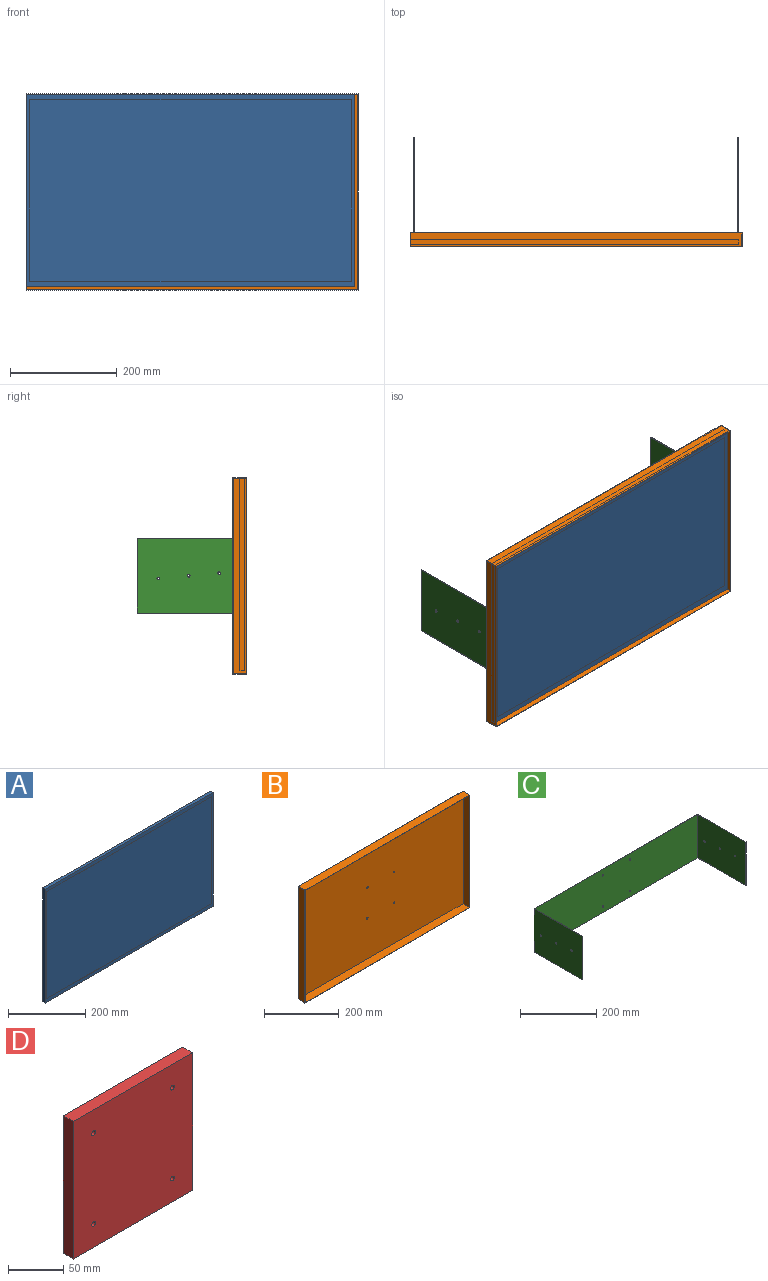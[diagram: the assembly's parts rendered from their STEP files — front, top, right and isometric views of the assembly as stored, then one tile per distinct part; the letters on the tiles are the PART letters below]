
ASSEMBLY  parts=4 mates=9
PART A: 11 faces, bbox 615.4x8.6x361.1 mm
  f0: plane 615.44x361.06mm, normal (0,1,0), area 222212.1mm2, adj f5,f6,f7,f8
  f1: plane 339.73x0.25mm, normal (1,0,0), area 86.3mm2, adj f2,f4,f9,f10
  f2: plane 603.25x0.25mm, normal (0,0,1), area 153.2mm2, adj f1,f3,f9,f10
  f3: plane 339.73x0.25mm, normal (-1,0,0), area 86.3mm2, adj f2,f4,f9,f10
  f4: plane 603.25x0.25mm, normal (0,0,-1), area 153.2mm2, adj f1,f3,f9,f10
  f5: plane 361.06x8.57mm, normal (-1,0,0), area 3095.2mm2, adj f0,f6,f8,f9
  f6: plane 615.44x8.57mm, normal (0,0,-1), area 5275.9mm2, adj f0,f5,f7,f9
  f7: plane 361.06x8.57mm, normal (1,0,0), area 3095.2mm2, adj f0,f6,f8,f9
  f8: plane 615.44x8.57mm, normal (0,0,1), area 5275.9mm2, adj f0,f5,f7,f9
  f9: plane 615.44x361.06mm, normal (0,-1,0), area 17273mm2, adj f1,f2,f3,f4,f5,f6,f7,f8
  f10: plane 603.25x339.73mm, normal (0,-1,0), area 204939.1mm2, adj f1,f2,f3,f4
PART B: 15 faces, bbox 622.3x26.2x368.3 mm
  f0: plane 622.3x26.16mm, normal (0,0,-1), area 16280.6mm2, adj f1,f3,f4,f9
  f1: plane 368.3x26.16mm, normal (1,0,0), area 9635.5mm2, adj f0,f2,f4,f9
  f2: plane 622.3x26.16mm, normal (0,0,1), area 16280.6mm2, adj f1,f3,f4,f9
  f3: plane 368.3x26.16mm, normal (-1,0,0), area 9635.5mm2, adj f0,f2,f4,f9
  f4: plane 622.3x368.3mm, normal (0,1,0), area 229121.8mm2, adj f0,f1,f2,f3,f11,f12,f13,f14
  f5: plane 620.78x25.4mm, normal (0,0,1), area 15767.7mm2, adj f6,f8,f9,f10
  f6: plane 366.78x25.4mm, normal (1,0,0), area 9316.1mm2, adj f5,f7,f9,f10
  f7: plane 620.78x25.4mm, normal (0,0,-1), area 15767.7mm2, adj f6,f8,f9,f10
  f8: plane 366.78x25.4mm, normal (-1,0,0), area 9316.1mm2, adj f5,f7,f9,f10
  f9: plane 622.3x368.3mm, normal (0,-1,0), area 1507.4mm2, adj f0,f1,f2,f3,f5,f6,f7,f8
  f10: plane 620.78x366.78mm, normal (0,-1,0), area 227614.5mm2, adj f5,f6,f7,f8,f11,f12,f13,f14
  f11: cylinder r=2.38mm len=4.76mm, axis (0,1,0), area 11.4mm2, adj f4,f10
  f12: cylinder r=2.38mm len=4.76mm, axis (0,1,0), area 11.4mm2, adj f4,f10
  f13: cylinder r=2.38mm len=4.76mm, axis (0,1,0), area 11.4mm2, adj f4,f10
  f14: cylinder r=2.38mm len=4.76mm, axis (0,1,0), area 11.4mm2, adj f4,f10
PART C: 20 faces, bbox 609.6x179x139.7 mm
  f0: plane 607.16x139.7mm, normal (0,-1,0), area 84749.2mm2, adj f2,f4,f6,f7,f8,f9,f10,f13
  f1: plane 179.02x139.7mm, normal (-1,0,0), area 24955.5mm2, adj f2,f4,f5,f11,f17,f18,f19
  f2: plane 609.6x179.02mm, normal (0,0,-1), area 1176.8mm2, adj f0,f1,f3,f5,f10,f11,f12,f13
  f3: plane 179.02x139.7mm, normal (1,0,0), area 24955.5mm2, adj f2,f4,f5,f12,f14,f15,f16
  f4: plane 609.6x179.02mm, normal (0,0,1), area 1176.8mm2, adj f0,f1,f3,f5,f10,f11,f12,f13
  f5: plane 609.6x139.7mm, normal (0,1,0), area 85089.9mm2, adj f1,f2,f3,f4,f6,f7,f8,f9
  f6: cylinder r=2.38mm len=4.76mm, axis (0,-1,0), area 18.2mm2, adj f0,f5
  f7: cylinder r=2.38mm len=4.76mm, axis (0,-1,0), area 18.2mm2, adj f0,f5
  f8: cylinder r=2.38mm len=4.76mm, axis (0,-1,0), area 18.2mm2, adj f0,f5
  f9: cylinder r=2.38mm len=4.76mm, axis (0,-1,0), area 18.2mm2, adj f0,f5
  f10: plane 177.8x139.7mm, normal (1,0,0), area 24785.2mm2, adj f0,f2,f4,f11,f17,f18,f19
  f11: plane 139.7x1.22mm, normal (0,-1,0), area 170.3mm2, adj f1,f2,f4,f10
  f12: plane 139.7x1.22mm, normal (0,-1,0), area 170.3mm2, adj f2,f3,f4,f13
  f13: plane 177.8x139.7mm, normal (-1,0,0), area 24785.2mm2, adj f0,f2,f4,f12,f14,f15,f16
  f14: cylinder r=2.38mm len=4.76mm, axis (1,0,0), area 18.2mm2, adj f3,f13
  f15: cylinder r=2.38mm len=4.76mm, axis (1,0,0), area 18.2mm2, adj f3,f13
  f16: cylinder r=2.38mm len=4.76mm, axis (1,0,0), area 18.2mm2, adj f3,f13
  f17: cylinder r=2.38mm len=4.76mm, axis (1,0,0), area 18.2mm2, adj f1,f10
  f18: cylinder r=2.38mm len=4.76mm, axis (1,0,0), area 18.2mm2, adj f1,f10
  f19: cylinder r=2.38mm len=4.76mm, axis (1,0,0), area 18.2mm2, adj f1,f10
PART D: 10 faces, bbox 152.4x12.7x152.4 mm
  f0: plane 152.4x12.7mm, normal (-1,0,0), area 1935.5mm2, adj f1,f3,f4,f5
  f1: plane 152.4x12.7mm, normal (0,0,-1), area 1935.5mm2, adj f0,f2,f4,f5
  f2: plane 152.4x12.7mm, normal (1,0,0), area 1935.5mm2, adj f1,f3,f4,f5
  f3: plane 152.4x12.7mm, normal (0,0,1), area 1935.5mm2, adj f0,f2,f4,f5
  f4: plane 152.4x152.4mm, normal (0,-1,0), area 23154.5mm2, adj f0,f1,f2,f3,f6,f7,f8,f9
  f5: plane 152.4x152.4mm, normal (0,1,0), area 23154.5mm2, adj f0,f1,f2,f3,f6,f7,f8,f9
  f6: cylinder r=2.38mm len=12.7mm, axis (0,-1,0), area 190mm2, adj f4,f5
  f7: cylinder r=2.38mm len=12.7mm, axis (0,-1,0), area 190mm2, adj f4,f5
  f8: cylinder r=2.38mm len=12.7mm, axis (0,-1,0), area 190mm2, adj f4,f5
  f9: cylinder r=2.38mm len=12.7mm, axis (0,-1,0), area 190mm2, adj f4,f5
PLACE A t=(-587.37,-440.9,42.39)mm
PLACE B t=(-273.55,-427.44,-144.61)mm
PLACE C rot(axis=(1,0,0),180deg) t=(-584.7,-427.44,39.96)mm
PLACE D t=(-584.7,-428.2,39.54)mm
MATE planar C.f5 <-> B.f4  axis (0,-1,0) through (-584.7,-427.44,39.96)mm
MATE planar D.f4 <-> A.f0  axis (0,-1,0) through (-660.9,-440.9,39.54)mm
MATE cylindrical C.f7 <-> B.f14  axis (0,1,0) through (-534.32,-426.22,89.92)mm
MATE cylindrical D.f7 <-> B.f13  axis (0,-1,0) through (-635.08,-440.9,-10.84)mm
MATE planar B.f10 <-> D.f5  axis (0,-1,0) through (-584.7,-428.2,39.54)mm
MATE planar B.f7 <-> A.f8  axis (0,0,-1) through (-584.7,-440.9,222.93)mm
MATE cylindrical D.f6 <-> B.f14  axis (0,-1,0) through (-534.32,-440.9,89.92)mm
MATE cylindrical C.f6 <-> B.f13  axis (0,1,0) through (-635.08,-426.22,-10.84)mm
MATE planar B.f6 <-> A.f5  axis (1,0,0) through (-895.09,-440.9,39.54)mm
